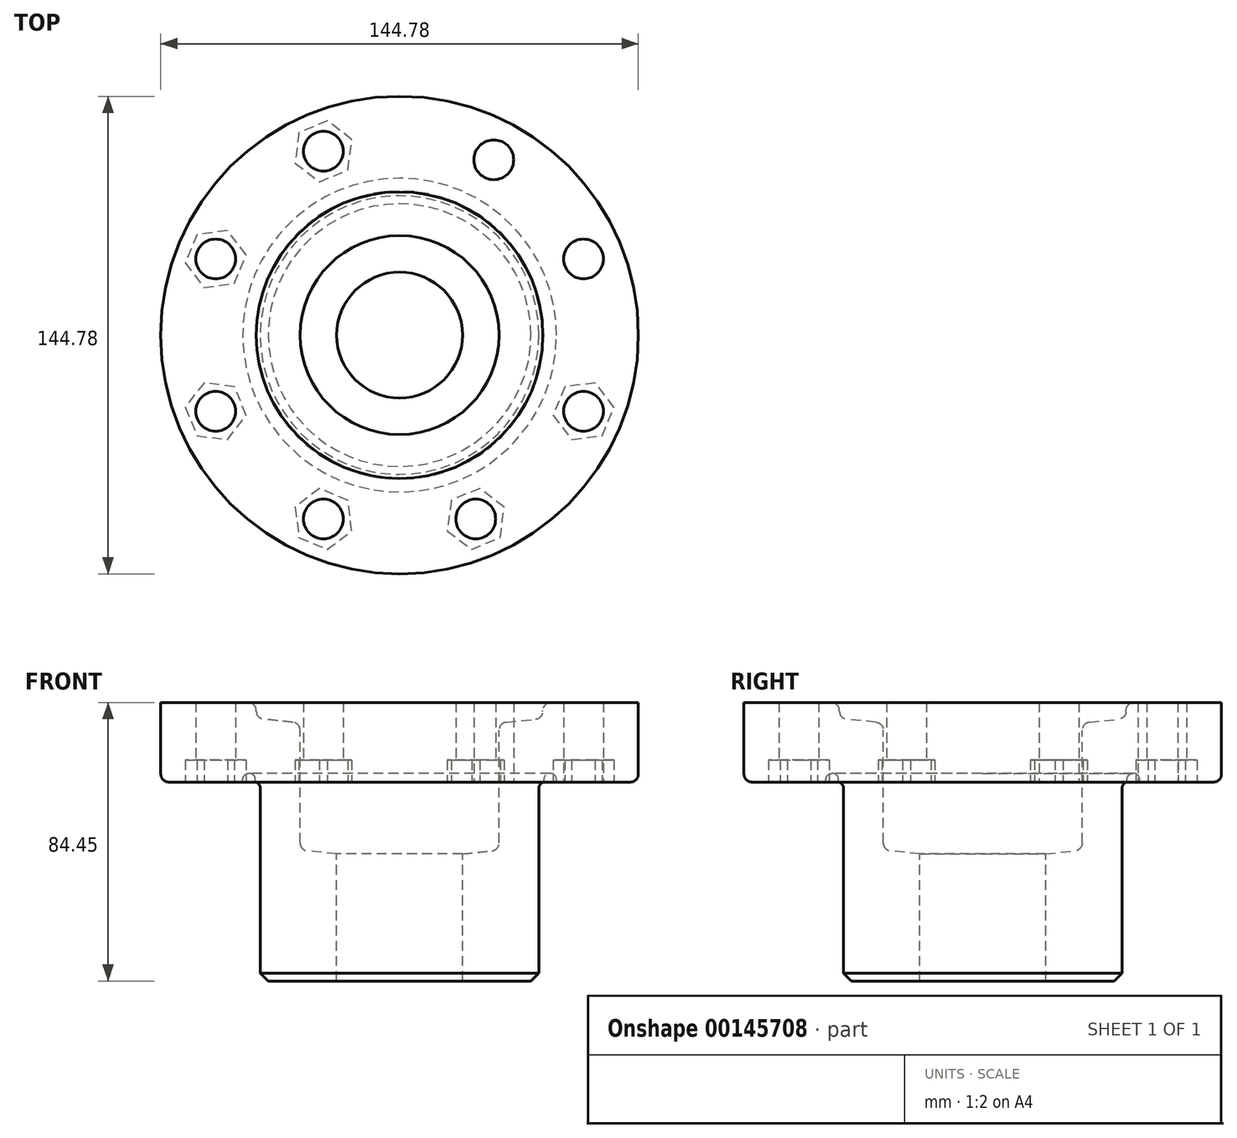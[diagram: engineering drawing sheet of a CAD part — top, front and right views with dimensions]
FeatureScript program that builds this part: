
annotation { "Feature Type Name" : "Feature", "Feature Type Description" : "" }
export const myFeature = defineFeature(function(context is Context, id is Id, definition is map)
    precondition{}
    {
        {
            var Q0;
            Q0=qCreatedBy(makeId("Front.planeOp"),FACE);
            var sketch = newSketch(context, id + "F0", { "sketchPlane" : qUnion([Q0])});
            skLineSegment(sketch, "E0", {"start": v(0, 75.35) * mm, "end": v(0, -76.8) * mm, "construction": true});
            skLineSegment(sketch, "E1", {"start": v(15.88, 69.4) * mm, "end": v(15.88, 49.12) * mm});
            skLineSegment(sketch, "E2", {"start": v(10.03, 48.5) * mm, "end": v(10.03, 28.21) * mm});
            skLineSegment(sketch, "E3", {"start": v(10.03, 28.21) * mm, "end": v(20.96, 28.21) * mm});
            skLineSegment(sketch, "E4", {"start": v(22.23, 29.48) * mm, "end": v(22.23, 59.96) * mm});
            skLineSegment(sketch, "E5", {"start": v(22.86, 70.12) * mm, "end": v(22.86, 72.66) * mm});
            skLineSegment(sketch, "E6", {"start": v(22.86, 72.66) * mm, "end": v(38.1, 72.66) * mm});
            skLineSegment(sketch, "E7", {"start": v(38.1, 72.66) * mm, "end": v(38.1, 59.96) * mm});
            skLineSegment(sketch, "E8", {"start": v(38.1, 59.96) * mm, "end": v(25.03, 59.96) * mm});
            skLineSegment(sketch, "E9", {"start": v(23, 59.96) * mm, "end": v(23, 61.36) * mm});
            skLineSegment(sketch, "E10", {"start": v(23, 61.36) * mm, "end": v(25.03, 61.36) * mm});
            skLineSegment(sketch, "E11", {"start": v(25.03, 61.36) * mm, "end": v(25.03, 59.96) * mm});
            skLineSegment(sketch, "E12.trimOffspring", {"start": v(23, 59.96) * mm, "end": v(22.23, 59.96) * mm});
            skLineSegment(sketch, "E13", {"start": v(20.96, 28.21) * mm, "end": v(22.23, 29.48) * mm});
            skPoint(sketch, "E14.start.orphan", {"position": v(22.23, 28.21) * mm});
            skLineSegment(sketch, "E15", {"start": v(22.86, 70.12) * mm, "end": v(15.88, 69.4) * mm});
            skLineSegment(sketch, "E16", {"start": v(15.88, 49.12) * mm, "end": v(10.03, 48.5) * mm});
            skSolve(sketch);
        }
        {
            var Q0;
            Q0=qSketchRegion(id+"F0",true);
            var Q1;
            Q1=sQuery(id+"F0.wireOp",EDGE,"E0");
            revolve(context, id + "F1", {"entities" : qUnion([Q0]), "axis" : qUnion([Q1]), "revolveType" : RevolveType.ONE_DIRECTION, "angle" : 360 * degree});
        }
        {
            var Q0;
            Q0=makeQuery(id+"F1.opRevolve","SWEPT_EDGE",EDGE,{"disambiguationData":[OSD([sQuery(id+"F0.wireOp",EDGE,"NfS8FBZc-bgWc-zHHI-cEcd-yeeJX1SY3rAC"),sQuery(id+"F0.wireOp",EDGE,"E5")])]});
            var Q1;
            Q1=makeQuery(id+"F1.opRevolve","SWEPT_EDGE",EDGE,{"disambiguationData":[OSD([sQuery(id+"F0.wireOp",EDGE,"E1"),sQuery(id+"F0.wireOp",EDGE,"bbtoYTUm-32SK-HFDn-8Iwu-w7CrsTeAnLED")])]});
            var Q2;
            Q2=makeQuery(id+"F1.opRevolve","SWEPT_EDGE",EDGE,{"disambiguationData":[OSD([sQuery(id+"F0.wireOp",EDGE,"E7"),sQuery(id+"F0.wireOp",EDGE,"E8")])]});
            fillet(context, id + "F2", {"entities" : qUnion([Q0, Q1, Q2]), "radius" : 1.27 * mm, "tangentPropagation" : true, "allowEdgeOverflow" : false});
        }
        {
            var Q0;
            Q0=makeQuery(id+"F1.opRevolve","SWEPT_EDGE",EDGE,{"disambiguationData":[OSD([sQuery(id+"F0.wireOp",EDGE,"E9"),sQuery(id+"F0.wireOp",EDGE,"E10")])]});
            var Q1;
            Q1=makeQuery(id+"F1.opRevolve","SWEPT_EDGE",EDGE,{"disambiguationData":[OSD([sQuery(id+"F0.wireOp",EDGE,"E10"),sQuery(id+"F0.wireOp",EDGE,"E11")])]});
            var Q2;
            Q2=makeQuery(id+"F1.opRevolve","SWEPT_EDGE",EDGE,{"disambiguationData":[OSD([sQuery(id+"F0.wireOp",EDGE,"E4"),sQuery(id+"F0.wireOp",EDGE,"E12.trimOffspring")])]});
            fillet(context, id + "F3", {"entities" : qUnion([Q0, Q1, Q2]), "radius" : 1.02 * mm, "tangentPropagation" : true, "allowEdgeOverflow" : false});
        }
        {
            var Q0;
            Q0=makeQuery(id+"F1.opRevolve","SWEPT_FACE",FACE,{"disambiguationData":[OSD([sQuery(id+"F0.wireOp",EDGE,"E6")])]});
            var sketch = newSketch(context, id + "F4", { "sketchPlane" : qUnion([Q0])});
            skCircle(sketch, "E17", {"center": v(-12.15, -29.33) * mm, "radius": 3.18 * mm});
            skCircle(sketch, "E18.1.0", {"center": v(12.15, -29.33) * mm, "radius": 3.18 * mm});
            skCircle(sketch, "E18.2.0", {"center": v(29.33, -12.15) * mm, "radius": 3.18 * mm});
            skCircle(sketch, "E18.5.0", {"center": v(-12.15, 29.33) * mm, "radius": 3.18 * mm});
            skCircle(sketch, "E18.6.0", {"center": v(-29.33, 12.15) * mm, "radius": 3.18 * mm});
            skCircle(sketch, "E18.7.0", {"center": v(-29.33, -12.15) * mm, "radius": 3.18 * mm});
            skPoint(sketch, "E18.center", {"position": v(0, 0) * mm});
            skCircle(sketch, "E19", {"center": v(15.02, 27.97) * mm, "radius": 3.18 * mm});
            skCircle(sketch, "E20", {"center": v(29.33, 12.15) * mm, "radius": 3.18 * mm});
            skSolve(sketch);
        }
        {
            var Q0;
            Q0=sQuery(id+"F4.wireOp",VERTEX,"E18.2.0.center");
            var Q1;
            Q1=sQuery(id+"F4.wireOp",VERTEX,"E18.1.0.center");
            var Q2;
            Q2=sQuery(id+"F4.wireOp",VERTEX,"E17.center");
            var Q3;
            Q3=sQuery(id+"F4.wireOp",VERTEX,"E18.7.0.center");
            var Q4;
            Q4=sQuery(id+"F4.wireOp",VERTEX,"E18.6.0.center");
            var Q5;
            Q5=sQuery(id+"F4.wireOp",VERTEX,"E18.5.0.center");
            var Q6;
            Q6=sQuery(id+"F4.wireOp",VERTEX,"E19.center");
            var Q7;
            Q7=sQuery(id+"F4.wireOp",VERTEX,"E20.center");
            var Q8;
            Q8=makeQuery(id+"F1.opRevolve","SWEPT_BODY",BODY,{"disambiguationData":[OSD([sQuery(id+"F0.wireOp",EDGE,"E1"),sQuery(id+"F0.wireOp",EDGE,"bbtoYTUm-32SK-HFDn-8Iwu-w7CrsTeAnLED"),sQuery(id+"F0.wireOp",EDGE,"E2"),sQuery(id+"F0.wireOp",EDGE,"E3"),sQuery(id+"F0.wireOp",EDGE,"E4"),sQuery(id+"F0.wireOp",EDGE,"NfS8FBZc-bgWc-zHHI-cEcd-yeeJX1SY3rAC"),sQuery(id+"F0.wireOp",EDGE,"E5"),sQuery(id+"F0.wireOp",EDGE,"E6"),sQuery(id+"F0.wireOp",EDGE,"E7"),sQuery(id+"F0.wireOp",EDGE,"E8"),sQuery(id+"F0.wireOp",EDGE,"E9"),sQuery(id+"F0.wireOp",EDGE,"E10"),sQuery(id+"F0.wireOp",EDGE,"E11"),sQuery(id+"F0.wireOp",EDGE,"E12.trimOffspring"),sQuery(id+"F0.wireOp",EDGE,"E13")])]});
            hole(context, id + "F5", {"style" : HoleStyle.SIMPLE, "endStyle" : HoleEndStyle.BLIND, "holeDiameter" : 6.35 * mm, "holeDepth" : 31.75 * mm, "locations" : qUnion([Q0, Q1, Q2, Q3, Q4, Q5, Q6, Q7]), "scope" : qUnion([Q8]), "startStyle" : HoleStartStyle.SKETCH});
        }
        {
            var Q0;
            Q0=makeQuery(id+"F1.opRevolve","SWEPT_FACE",FACE,{"disambiguationData":[OSD([sQuery(id+"F0.wireOp",EDGE,"E8")])]});
            var sketch = newSketch(context, id + "F6", { "sketchPlane" : qUnion([Q0])});
            skCircle(sketch, "E21.cCircle", {"center": v(-12.15, -29.33) * mm, "radius": 4.25 * mm, "construction": true});
            skLineSegment(sketch, "E21.0", {"start": v(-12.8, -24.47) * mm, "end": v(-8.26, -26.35) * mm});
            skLineSegment(sketch, "E21.1", {"start": v(-8.26, -26.35) * mm, "end": v(-7.62, -31.21) * mm});
            skLineSegment(sketch, "E21.2", {"start": v(-7.62, -31.21) * mm, "end": v(-11.5, -34.2) * mm});
            skLineSegment(sketch, "E21.3", {"start": v(-11.5, -34.2) * mm, "end": v(-16.04, -32.32) * mm});
            skLineSegment(sketch, "E21.4", {"start": v(-16.04, -32.32) * mm, "end": v(-16.68, -27.46) * mm});
            skLineSegment(sketch, "E21.5", {"start": v(-16.68, -27.46) * mm, "end": v(-12.8, -24.47) * mm});
            skPoint(sketch, "E21.0.midPoint", {"position": v(-10.52, -25.4) * mm});
            skCircle(sketch, "E22.cCircle", {"center": v(-29.33, -12.15) * mm, "radius": 4.25 * mm, "construction": true});
            skLineSegment(sketch, "E22.0", {"start": v(-26.35, -8.26) * mm, "end": v(-24.47, -12.8) * mm});
            skLineSegment(sketch, "E22.1", {"start": v(-24.47, -12.8) * mm, "end": v(-27.46, -16.68) * mm});
            skLineSegment(sketch, "E22.2", {"start": v(-27.46, -16.68) * mm, "end": v(-32.32, -16.04) * mm});
            skLineSegment(sketch, "E22.3", {"start": v(-32.32, -16.04) * mm, "end": v(-34.2, -11.5) * mm});
            skLineSegment(sketch, "E22.4", {"start": v(-34.2, -11.5) * mm, "end": v(-31.21, -7.62) * mm});
            skLineSegment(sketch, "E22.5", {"start": v(-31.21, -7.62) * mm, "end": v(-26.35, -8.26) * mm});
            skPoint(sketch, "E22.0.midPoint", {"position": v(-25.4, -10.52) * mm});
            skCircle(sketch, "E23.cCircle", {"center": v(-29.33, 12.15) * mm, "radius": 4.25 * mm, "construction": true});
            skLineSegment(sketch, "E23.0", {"start": v(-24.47, 12.8) * mm, "end": v(-26.35, 8.26) * mm});
            skLineSegment(sketch, "E23.1", {"start": v(-26.35, 8.26) * mm, "end": v(-31.21, 7.62) * mm});
            skLineSegment(sketch, "E23.2", {"start": v(-31.21, 7.62) * mm, "end": v(-34.2, 11.5) * mm});
            skLineSegment(sketch, "E23.3", {"start": v(-34.2, 11.5) * mm, "end": v(-32.32, 16.04) * mm});
            skLineSegment(sketch, "E23.4", {"start": v(-32.32, 16.04) * mm, "end": v(-27.46, 16.68) * mm});
            skLineSegment(sketch, "E23.5", {"start": v(-27.46, 16.68) * mm, "end": v(-24.47, 12.8) * mm});
            skPoint(sketch, "E23.0.midPoint", {"position": v(-25.4, 10.52) * mm});
            skCircle(sketch, "E24.cCircle", {"center": v(-12.15, 29.33) * mm, "radius": 4.25 * mm, "construction": true});
            skLineSegment(sketch, "E24.0", {"start": v(-8.26, 26.35) * mm, "end": v(-12.8, 24.47) * mm});
            skLineSegment(sketch, "E24.1", {"start": v(-12.8, 24.47) * mm, "end": v(-16.68, 27.46) * mm});
            skLineSegment(sketch, "E24.2", {"start": v(-16.68, 27.46) * mm, "end": v(-16.04, 32.32) * mm});
            skLineSegment(sketch, "E24.3", {"start": v(-16.04, 32.32) * mm, "end": v(-11.5, 34.2) * mm});
            skLineSegment(sketch, "E24.4", {"start": v(-11.5, 34.2) * mm, "end": v(-7.62, 31.21) * mm});
            skLineSegment(sketch, "E24.5", {"start": v(-7.62, 31.21) * mm, "end": v(-8.26, 26.35) * mm});
            skPoint(sketch, "E24.0.midPoint", {"position": v(-10.52, 25.4) * mm});
            skCircle(sketch, "E25.cCircle", {"center": v(12.15, 29.33) * mm, "radius": 4.25 * mm, "construction": true});
            skLineSegment(sketch, "E25.0", {"start": v(12.8, 24.47) * mm, "end": v(8.26, 26.35) * mm});
            skLineSegment(sketch, "E25.1", {"start": v(8.26, 26.35) * mm, "end": v(7.62, 31.21) * mm});
            skLineSegment(sketch, "E25.2", {"start": v(7.62, 31.21) * mm, "end": v(11.5, 34.2) * mm});
            skLineSegment(sketch, "E25.3", {"start": v(11.5, 34.2) * mm, "end": v(16.04, 32.32) * mm});
            skLineSegment(sketch, "E25.4", {"start": v(16.04, 32.32) * mm, "end": v(16.68, 27.46) * mm});
            skLineSegment(sketch, "E25.5", {"start": v(16.68, 27.46) * mm, "end": v(12.8, 24.47) * mm});
            skPoint(sketch, "E25.0.midPoint", {"position": v(10.52, 25.4) * mm});
            skCircle(sketch, "E26.cCircle", {"center": v(29.33, 12.15) * mm, "radius": 4.25 * mm, "construction": true});
            skLineSegment(sketch, "E26.0", {"start": v(26.35, 8.26) * mm, "end": v(24.47, 12.8) * mm});
            skLineSegment(sketch, "E26.1", {"start": v(24.47, 12.8) * mm, "end": v(27.46, 16.68) * mm});
            skLineSegment(sketch, "E26.2", {"start": v(27.46, 16.68) * mm, "end": v(32.32, 16.04) * mm});
            skLineSegment(sketch, "E26.3", {"start": v(32.32, 16.04) * mm, "end": v(34.2, 11.5) * mm});
            skLineSegment(sketch, "E26.4", {"start": v(34.2, 11.5) * mm, "end": v(31.21, 7.62) * mm});
            skLineSegment(sketch, "E26.5", {"start": v(31.21, 7.62) * mm, "end": v(26.35, 8.26) * mm});
            skPoint(sketch, "E26.0.midPoint", {"position": v(25.4, 10.52) * mm});
            skSolve(sketch);
        }
        {
            var Q0;
            Q0=qSketchRegion(id+"F6",true);
            extrude(context, id + "F7", {"entities" : qUnion([Q0]), "operationType" : NewBodyOperationType.REMOVE, "oppositeDirection" : true, "depth" : 3.5 * mm});
        }
        {
            var Q0;
            Q0=qSketchRegion(id+"F6",true);
            extrude(context, id + "F8", {"entities" : qUnion([Q0]), "operationType" : NewBodyOperationType.REMOVE, "oppositeDirection" : true, "depth" : 3.5 * mm});
        }
        {
            var Q0;
            Q0=makeQuery(id+"F1.opRevolve","SWEPT_BODY",BODY,{"disambiguationData":[OSD([sQuery(id+"F0.wireOp",EDGE,"E1"),sQuery(id+"F0.wireOp",EDGE,"E2"),sQuery(id+"F0.wireOp",EDGE,"E3"),sQuery(id+"F0.wireOp",EDGE,"E4"),sQuery(id+"F0.wireOp",EDGE,"E5"),sQuery(id+"F0.wireOp",EDGE,"E6"),sQuery(id+"F0.wireOp",EDGE,"E7"),sQuery(id+"F0.wireOp",EDGE,"E8"),sQuery(id+"F0.wireOp",EDGE,"E9"),sQuery(id+"F0.wireOp",EDGE,"E10"),sQuery(id+"F0.wireOp",EDGE,"E11"),sQuery(id+"F0.wireOp",EDGE,"E12.trimOffspring"),sQuery(id+"F0.wireOp",EDGE,"E13"),sQuery(id+"F0.wireOp",EDGE,"E15"),sQuery(id+"F0.wireOp",EDGE,"E16")])]});
            var Q1;
            Q1=qCreatedBy(makeId("Origin.pointOp"),VERTEX);
            transform(context, id + "F9", {"entities" : qUnion([Q0]), "transformType" : TransformType.SCALE_UNIFORMLY, "scale" : 1.9, "scalePoint" : qUnion([Q1]), "makeCopy" : false});
        }
    });
